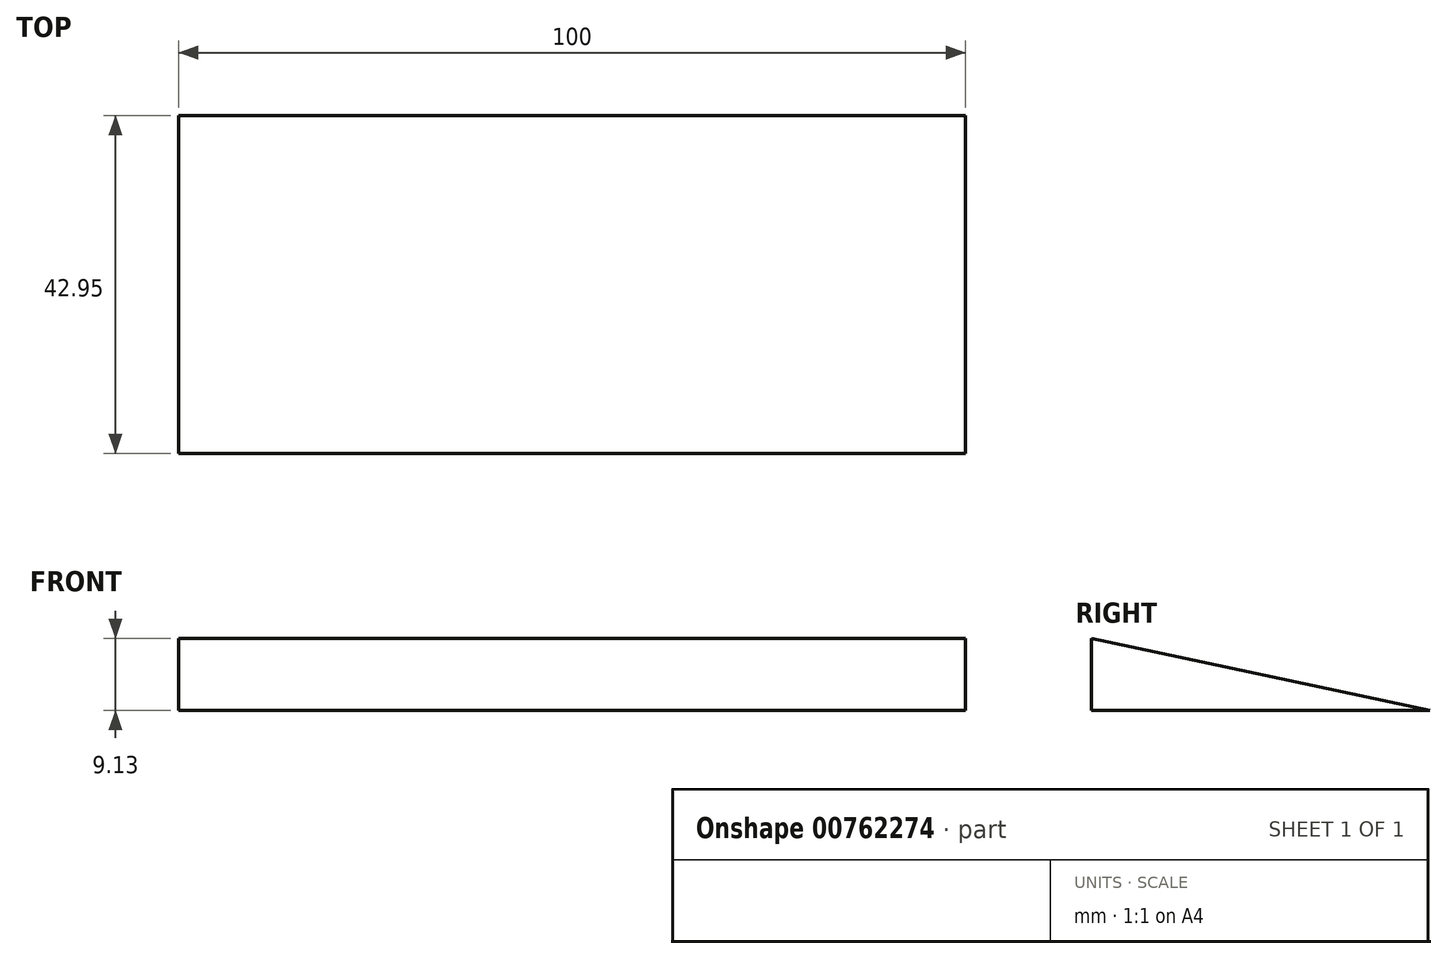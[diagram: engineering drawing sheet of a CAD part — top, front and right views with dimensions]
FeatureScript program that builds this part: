
annotation { "Feature Type Name" : "Feature", "Feature Type Description" : "" }
export const myFeature = defineFeature(function(context is Context, id is Id, definition is map)
    precondition{}
    {
        {
            var Q0;
            Q0=qCreatedBy(makeId("Right.planeOp"),FACE);
            var sketch = newSketch(context, id + "F0", { "sketchPlane" : qUnion([Q0])});
            skLineSegment(sketch, "E0", {"start": v(0, 0) * mm, "end": v(-42.95, 0) * mm});
            skLineSegment(sketch, "E1", {"start": v(-42.95, 0) * mm, "end": v(-42.95, 9.13) * mm});
            skLineSegment(sketch, "E2", {"start": v(-42.95, 9.13) * mm, "end": v(0, 0) * mm});
            skLineSegment(sketch, "E3", {"start": v(-42.95, 9.13) * mm, "end": v(-42.95, 29.13) * mm, "construction": true});
            skLineSegment(sketch, "E4", {"start": v(-5.78, 1.23) * mm, "end": v(-5.78, 21.23) * mm, "construction": true});
            skLineSegment(sketch, "E5", {"start": v(0, 0) * mm, "end": v(0, 42.98) * mm, "construction": true});
            skLineSegment(sketch, "E6", {"start": v(-62.95, 0) * mm, "end": v(-62.95, 52.74) * mm, "construction": true});
            skLineSegment(sketch, "E7", {"start": v(-62.95, 0) * mm, "end": v(-42.95, 0) * mm, "construction": true});
            skLineSegment(sketch, "E8", {"start": v(-5.78, 21.23) * mm, "end": v(0, 0) * mm, "construction": true});
            skCircle(sketch, "E9", {"center": v(-13.82, 12.71) * mm, "radius": 10 * mm, "construction": true});
            skLineSegment(sketch, "E10", {"start": v(-24.36, 25.18) * mm, "end": v(-24.36, 5.18) * mm, "construction": true});
            skLineSegment(sketch, "E11", {"start": v(-11.74, 22.5) * mm, "end": v(-42.95, 29.13) * mm, "construction": true});
            skSolve(sketch);
        }
        {
            var Q0;
            Q0=makeQuery(id+"F0.imprint","IMPRINT",FACE,{"disambiguationData":[TD([[makeQuery(id+"F0.imprint","IMPRINT",EDGE,{"derivedFrom":sQuery(id+"F0.wireOp",EDGE,"E0")}),-1.0]])]});
            extrude(context, id + "F1", {"entities" : qUnion([Q0]), "depth" : 100 * mm, "offsetDistance" : 25 * mm});
        }
    });
